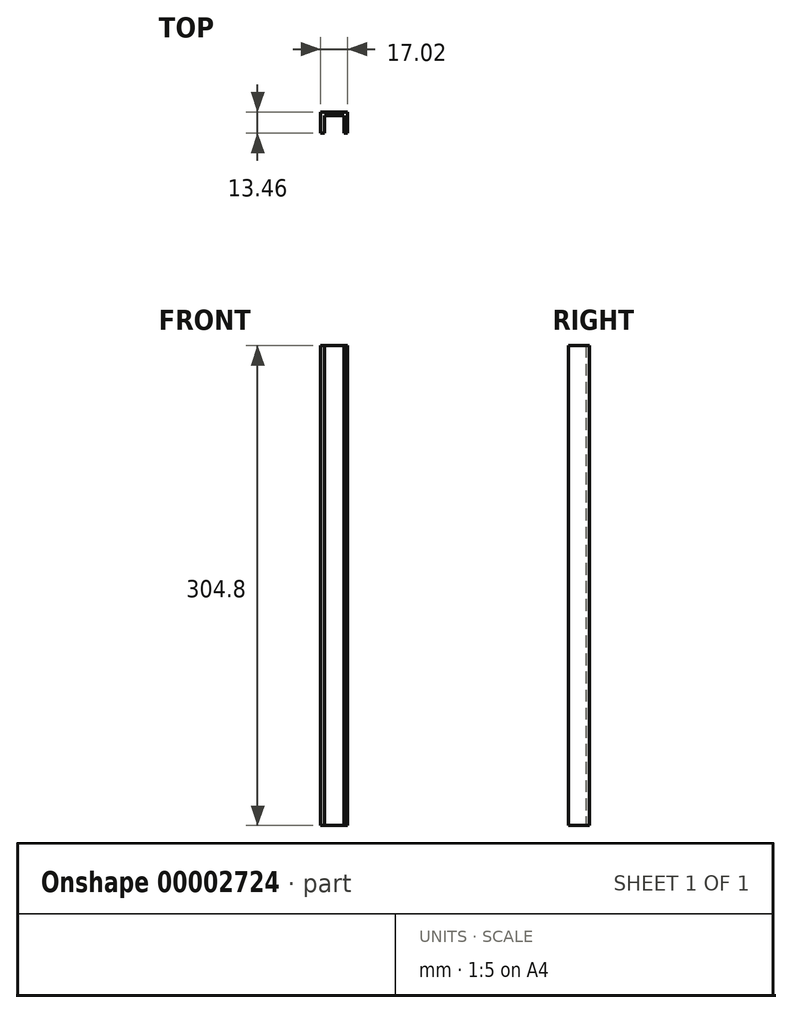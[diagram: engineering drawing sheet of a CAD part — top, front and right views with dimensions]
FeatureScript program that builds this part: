
annotation { "Feature Type Name" : "Feature", "Feature Type Description" : "" }
export const myFeature = defineFeature(function(context is Context, id is Id, definition is map)
    precondition{}
    {
        {
            var Q0;
            Q0=qCreatedBy(makeId("Top.planeOp"),FACE);
            var sketch = newSketch(context, id + "F0", { "sketchPlane" : qUnion([Q0])});
            skLineSegment(sketch, "E0", {"start": v(0, 0) * mm, "end": v(17.02, 0) * mm});
            skLineSegment(sketch, "E1", {"start": v(17.02, 0) * mm, "end": v(17.02, -13.46) * mm});
            skLineSegment(sketch, "E2", {"start": v(17.02, -13.46) * mm, "end": v(14.73, -13.46) * mm});
            skLineSegment(sketch, "E3", {"start": v(14.73, -13.46) * mm, "end": v(14.73, -2.29) * mm});
            skLineSegment(sketch, "E4", {"start": v(14.73, -2.29) * mm, "end": v(2.29, -2.29) * mm});
            skLineSegment(sketch, "E5", {"start": v(2.29, -2.29) * mm, "end": v(2.29, -13.46) * mm});
            skLineSegment(sketch, "E6", {"start": v(2.29, -13.46) * mm, "end": v(0, -13.46) * mm});
            skLineSegment(sketch, "E7", {"start": v(0, -13.46) * mm, "end": v(0, 0) * mm});
            skSolve(sketch);
        }
        {
            var Q0;
            Q0=makeQuery(id+"F0.imprint","IMPRINT",FACE,{"disambiguationData":[TD([[makeQuery(id+"F0.imprint","IMPRINT",EDGE,{"derivedFrom":sQuery(id+"F0.wireOp",EDGE,"E0")}),-1.0]])]});
            extrude(context, id + "F1", {"entities" : qUnion([Q0]), "depth" : 304.8 * mm});
        }
    });
